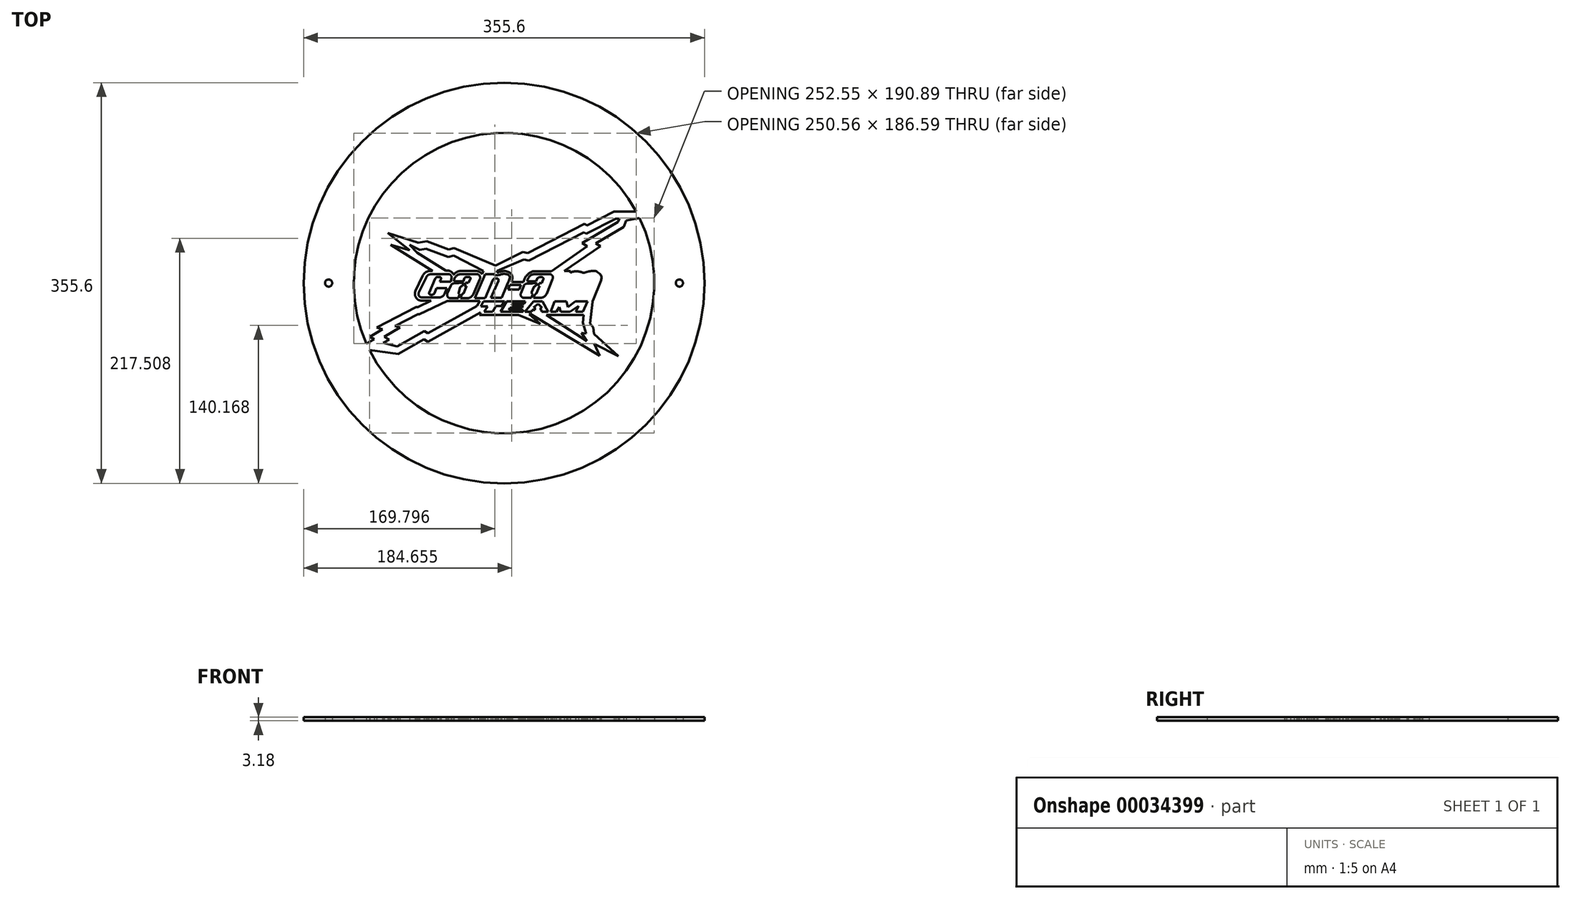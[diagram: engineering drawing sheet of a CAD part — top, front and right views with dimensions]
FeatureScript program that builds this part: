
annotation { "Feature Type Name" : "Feature", "Feature Type Description" : "" }
export const myFeature = defineFeature(function(context is Context, id is Id, definition is map)
    precondition{}
    {
        {
            var Q0;
            Q0=qCreatedBy(makeId("Top.planeOp"),FACE);
            var sketch = newSketch(context, id + "F0", { "sketchPlane" : qUnion([Q0])});
            skCircle(sketch, "E0", {"center": v(0, -177.8) * mm, "radius": 177.8 * mm});
            skArc(sketch, "E1.0", {"start": v(117.28, -114.33) * mm, "mid": v(-58.58, -58) * mm, "end": v(-122.11, -231.38) * mm});
            skLineSegment(sketch, "E2", {"start": v(-72.26, -171.41) * mm, "end": v(-78.52, -184.98) * mm});
            skLineSegment(sketch, "E3", {"start": v(117.28, -114.33) * mm, "end": v(97.65, -114.33) * mm});
            skLineSegment(sketch, "E4", {"start": v(97.65, -114.33) * mm, "end": v(73.49, -126.6) * mm});
            skLineSegment(sketch, "E5", {"start": v(73.49, -126.6) * mm, "end": v(71.57, -125.24) * mm});
            skLineSegment(sketch, "E6", {"start": v(71.57, -125.24) * mm, "end": v(21.06, -151.12) * mm});
            skLineSegment(sketch, "E7", {"start": v(21.06, -151.12) * mm, "end": v(16.63, -150.13) * mm});
            skLineSegment(sketch, "E8", {"start": v(16.63, -150.13) * mm, "end": v(-7.54, -162.28) * mm});
            skLineSegment(sketch, "E9", {"start": v(-7.54, -162.28) * mm, "end": v(-44.28, -146.75) * mm});
            skLineSegment(sketch, "E10", {"start": v(-44.28, -146.75) * mm, "end": v(-49.08, -148.1) * mm});
            skLineSegment(sketch, "E11", {"start": v(-49.08, -148.1) * mm, "end": v(-68.43, -140.65) * mm});
            skLineSegment(sketch, "E12", {"start": v(-68.43, -140.65) * mm, "end": v(-76.04, -142.13) * mm});
            skLineSegment(sketch, "E13", {"start": v(-76.04, -142.13) * mm, "end": v(-102.97, -133.39) * mm});
            skLineSegment(sketch, "E14", {"start": v(-102.97, -133.39) * mm, "end": v(-83.66, -148.7) * mm});
            skLineSegment(sketch, "E15", {"start": v(-83.66, -148.7) * mm, "end": v(-100.42, -143.93) * mm});
            skLineSegment(sketch, "E16", {"start": v(-100.42, -143.93) * mm, "end": v(-63.27, -167) * mm});
            skLineSegment(sketch, "E17", {"start": v(-63.27, -167) * mm, "end": v(-65.35, -167) * mm});
            skArc(sketch, "E18", {"start": v(-65.35, -167) * mm, "mid": v(-69.45, -168.2) * mm, "end": v(-72.26, -171.41) * mm});
            skLineSegment(sketch, "E19", {"start": v(-64.55, -193.44) * mm, "end": v(-73.1, -193.44) * mm});
            skArc(sketch, "E20", {"start": v(-78.52, -184.98) * mm, "mid": v(-78.13, -190.7) * mm, "end": v(-73.1, -193.44) * mm});
            skLineSegment(sketch, "E21", {"start": v(-107.77, -218.97) * mm, "end": v(-112.88, -217.3) * mm});
            skLineSegment(sketch, "E22", {"start": v(-107.77, -218.97) * mm, "end": v(-119.02, -225.44) * mm});
            skLineSegment(sketch, "E23", {"start": v(-119.02, -225.44) * mm, "end": v(-115.05, -227.68) * mm});
            skLineSegment(sketch, "E24", {"start": v(-119.42, -237.14) * mm, "end": v(-93.78, -240.85) * mm});
            skLineSegment(sketch, "E25", {"start": v(-93.78, -240.85) * mm, "end": v(-70.85, -227.83) * mm});
            skLineSegment(sketch, "E26", {"start": v(-70.85, -227.83) * mm, "end": v(-67.64, -229.84) * mm});
            skLineSegment(sketch, "E27", {"start": v(-67.64, -229.84) * mm, "end": v(-20.79, -203.8) * mm});
            skLineSegment(sketch, "E28", {"start": v(-20.79, -203.8) * mm, "end": v(-21.82, -205.96) * mm});
            skLineSegment(sketch, "E29", {"start": v(-21.82, -205.96) * mm, "end": v(12.97, -205.96) * mm});
            skLineSegment(sketch, "E30", {"start": v(85.4, -145.02) * mm, "end": v(53.44, -167.15) * mm});
            skLineSegment(sketch, "E31", {"start": v(85.4, -145.02) * mm, "end": v(81.53, -142.54) * mm});
            skLineSegment(sketch, "E32", {"start": v(81.53, -142.54) * mm, "end": v(106.14, -127.9) * mm});
            skLineSegment(sketch, "E33", {"start": v(106.14, -127.9) * mm, "end": v(108.41, -122.44) * mm});
            skLineSegment(sketch, "E34", {"start": v(108.41, -122.44) * mm, "end": v(120.17, -119.99) * mm});
            skArc(sketch, "E35.trimOffspring", {"start": v(-119.42, -237.14) * mm, "mid": v(58.58, -297.6) * mm, "end": v(120.17, -119.99) * mm});
            skLineSegment(sketch, "E36", {"start": v(-115.05, -227.68) * mm, "end": v(-122.11, -231.38) * mm});
            skLineSegment(sketch, "E37", {"start": v(-64.55, -193.44) * mm, "end": v(-76.52, -199) * mm});
            skLineSegment(sketch, "E38", {"start": v(-76.52, -199) * mm, "end": v(-77.85, -199) * mm});
            skLineSegment(sketch, "E39", {"start": v(-77.85, -199) * mm, "end": v(-112.88, -217.3) * mm});
            skLineSegment(sketch, "E40", {"start": v(12.97, -205.96) * mm, "end": v(32.12, -214.14) * mm});
            skLineSegment(sketch, "E41", {"start": v(32.12, -214.14) * mm, "end": v(22.38, -205.4) * mm});
            skLineSegment(sketch, "E42", {"start": v(22.38, -205.4) * mm, "end": v(23.2, -205.1) * mm});
            skLineSegment(sketch, "E43", {"start": v(23.2, -205.1) * mm, "end": v(84.9, -242.25) * mm});
            skLineSegment(sketch, "E44", {"start": v(84.9, -242.25) * mm, "end": v(80.04, -231.96) * mm});
            skLineSegment(sketch, "E45", {"start": v(76.25, -213.75) * mm, "end": v(78.4, -194.42) * mm});
            skLineSegment(sketch, "E46", {"start": v(78.7, -193.29) * mm, "end": v(86, -175.37) * mm});
            skLineSegment(sketch, "E47", {"start": v(53.44, -167.15) * mm, "end": v(58.86, -167.15) * mm});
            skLineSegment(sketch, "E48", {"start": v(58.86, -167.15) * mm, "end": v(58.86, -168.66) * mm});
            skArc(sketch, "E49", {"start": v(70.01, -168.75) * mm, "mid": v(64.45, -167.37) * mm, "end": v(58.86, -168.66) * mm});
            skFitSpline(sketch, "E50", {"points": [v(70.01, -168.75) * mm, v(76.95, -167.16) * mm, v(82.12, -167.61) * mm, v(86.22, -171.54) * mm, v(86, -175.37) * mm], "startDerivative": vector(25.34, 5.48) * mm, "endDerivative": vector(-7.42, -18.3) * mm});
            skLineSegment(sketch, "E51.0", {"start": v(-67.47, -222.43) * mm, "end": v(-23.9, -198.21) * mm});
            skLineSegment(sketch, "E51.1", {"start": v(-70.72, -220.4) * mm, "end": v(-67.47, -222.43) * mm});
            skLineSegment(sketch, "E51.2", {"start": v(-94.7, -234.01) * mm, "end": v(-70.72, -220.4) * mm});
            skLineSegment(sketch, "E52.0", {"start": v(-101.76, -227.87) * mm, "end": v(-107.29, -230.78) * mm});
            skLineSegment(sketch, "E52.1", {"start": v(-106.18, -225.38) * mm, "end": v(-101.76, -227.87) * mm});
            skLineSegment(sketch, "E52.2", {"start": v(-92.25, -217.37) * mm, "end": v(-106.18, -225.38) * mm});
            skLineSegment(sketch, "E52.3", {"start": v(-50.27, -193.82) * mm, "end": v(-75.12, -205.35) * mm});
            skLineSegment(sketch, "E52.4", {"start": v(-75.12, -205.35) * mm, "end": v(-76.3, -205.35) * mm});
            skLineSegment(sketch, "E52.5", {"start": v(-76.3, -205.35) * mm, "end": v(-96.6, -215.95) * mm});
            skLineSegment(sketch, "E52.6", {"start": v(-92.25, -217.37) * mm, "end": v(-96.6, -215.95) * mm});
            skLineSegment(sketch, "E53.trimOffspring", {"start": v(-107.29, -230.78) * mm, "end": v(-94.7, -234.01) * mm});
            skLineSegment(sketch, "E54.0", {"start": v(73.94, -145.23) * mm, "end": v(42.04, -167.32) * mm});
            skLineSegment(sketch, "E54.2", {"start": v(101.09, -123.52) * mm, "end": v(102.27, -120.68) * mm});
            skLineSegment(sketch, "E54.3", {"start": v(69.42, -142.35) * mm, "end": v(101.09, -123.52) * mm});
            skLineSegment(sketch, "E54.4", {"start": v(73.94, -145.23) * mm, "end": v(69.42, -142.35) * mm});
            skLineSegment(sketch, "E55.0", {"start": v(-69.01, -147.23) * mm, "end": v(-74.83, -148.36) * mm});
            skLineSegment(sketch, "E55.1", {"start": v(-49.39, -154.78) * mm, "end": v(-69.01, -147.23) * mm});
            skLineSegment(sketch, "E55.2", {"start": v(-44.7, -153.46) * mm, "end": v(-49.39, -154.78) * mm});
            skLineSegment(sketch, "E55.3", {"start": v(-18.2, -167.21) * mm, "end": v(-44.7, -153.46) * mm});
            skLineSegment(sketch, "E55.4", {"start": v(17.46, -156.82) * mm, "end": v(-6.17, -167.21) * mm});
            skLineSegment(sketch, "E55.5", {"start": v(21.92, -157.81) * mm, "end": v(17.46, -156.82) * mm});
            skLineSegment(sketch, "E55.7", {"start": v(99.17, -120.68) * mm, "end": v(72.95, -133.99) * mm});
            skLineSegment(sketch, "E55.8", {"start": v(72.95, -133.99) * mm, "end": v(71.04, -132.64) * mm});
            skLineSegment(sketch, "E55.9", {"start": v(71.04, -132.64) * mm, "end": v(21.92, -157.81) * mm});
            skLineSegment(sketch, "E56.trimOffspring", {"start": v(102.27, -120.68) * mm, "end": v(99.17, -120.68) * mm});
            skLineSegment(sketch, "E57.0", {"start": v(-77.12, -150.92) * mm, "end": v(-51.5, -166.82) * mm});
            skLineSegment(sketch, "E58", {"start": v(-18.2, -167.21) * mm, "end": v(-6.17, -167.21) * mm});
            skLineSegment(sketch, "E59", {"start": v(-77.12, -150.92) * mm, "end": v(-83.81, -143.85) * mm});
            skLineSegment(sketch, "E60", {"start": v(-83.81, -143.85) * mm, "end": v(-74.83, -148.36) * mm});
            skLineSegment(sketch, "E61", {"start": v(-51.5, -166.82) * mm, "end": v(-49.7, -166.82) * mm});
            skLineSegment(sketch, "E62", {"start": v(-38.6, -167.12) * mm, "end": v(-24.39, -167.12) * mm});
            skLineSegment(sketch, "E63", {"start": v(25.57, -167.32) * mm, "end": v(42.04, -167.32) * mm});
            skLineSegment(sketch, "E64", {"start": v(-44.94, -170.34) * mm, "end": v(-44.36, -170.34) * mm});
            skArc(sketch, "E65", {"start": v(-38.6, -167.12) * mm, "mid": v(-41.9, -167.98) * mm, "end": v(-44.36, -170.34) * mm});
            skArc(sketch, "E66", {"start": v(-44.94, -170.34) * mm, "mid": v(-46.74, -167.8) * mm, "end": v(-49.7, -166.82) * mm});
            skLineSegment(sketch, "E67", {"start": v(-18.2, -167.21) * mm, "end": v(-19.63, -169.96) * mm});
            skArc(sketch, "E68", {"start": v(-19.63, -169.96) * mm, "mid": v(-21.62, -167.88) * mm, "end": v(-24.39, -167.12) * mm});
            skLineSegment(sketch, "E69", {"start": v(-6.17, -167.21) * mm, "end": v(-6.17, -168.44) * mm});
            skLineSegment(sketch, "E70", {"start": v(17.18, -176.77) * mm, "end": v(6.63, -176.77) * mm});
            skLineSegment(sketch, "E71", {"start": v(6.63, -176.77) * mm, "end": v(7.12, -175.68) * mm});
            skLineSegment(sketch, "E72", {"start": v(17.18, -176.77) * mm, "end": v(17.56, -175.58) * mm});
            skArc(sketch, "E73", {"start": v(25.57, -167.32) * mm, "mid": v(20.6, -170.52) * mm, "end": v(17.56, -175.58) * mm});
            skFitSpline(sketch, "E74", {"points": [v(-6.17, -168.44) * mm, v(-1.73, -167.3) * mm, v(3.35, -167.7) * mm, v(7.07, -170.88) * mm, v(7.12, -175.68) * mm], "startDerivative": vector(17.75, 5.69) * mm, "endDerivative": vector(-3.32, -20.38) * mm});
            skLineSegment(sketch, "E75", {"start": v(-50.27, -193.82) * mm, "end": v(-21.3, -193.82) * mm});
            skLineSegment(sketch, "E76", {"start": v(-21.3, -193.82) * mm, "end": v(-23.9, -198.21) * mm});
            skLineSegment(sketch, "E77", {"start": v(-18.13, -194) * mm, "end": v(-20.4, -198.54) * mm});
            skLineSegment(sketch, "E78", {"start": v(-20.4, -198.54) * mm, "end": v(-14.6, -198.54) * mm});
            skLineSegment(sketch, "E79", {"start": v(-14.6, -198.54) * mm, "end": v(-17.8, -203.32) * mm});
            skLineSegment(sketch, "E80", {"start": v(-17.8, -203.32) * mm, "end": v(-10.12, -203.32) * mm});
            skLineSegment(sketch, "E81", {"start": v(-10.12, -203.32) * mm, "end": v(-7.03, -198.16) * mm});
            skLineSegment(sketch, "E82", {"start": v(-7.03, -198.16) * mm, "end": v(-2.13, -198.16) * mm});
            skLineSegment(sketch, "E83", {"start": v(-2.13, -198.16) * mm, "end": v(0.4, -194) * mm});
            skLineSegment(sketch, "E84", {"start": v(0.4, -194) * mm, "end": v(-18.13, -194) * mm});
            skLineSegment(sketch, "E85", {"start": v(2.48, -194) * mm, "end": v(-3.15, -203.32) * mm});
            skLineSegment(sketch, "E86", {"start": v(-3.15, -203.32) * mm, "end": v(16.87, -203.32) * mm});
            skLineSegment(sketch, "E87", {"start": v(16.87, -203.32) * mm, "end": v(16.87, -201.77) * mm});
            skLineSegment(sketch, "E88", {"start": v(16.87, -201.77) * mm, "end": v(4.38, -201.77) * mm});
            skLineSegment(sketch, "E89", {"start": v(4.38, -201.77) * mm, "end": v(5.34, -199.65) * mm});
            skLineSegment(sketch, "E90", {"start": v(5.34, -199.65) * mm, "end": v(16.08, -199.65) * mm});
            skLineSegment(sketch, "E91", {"start": v(16.08, -199.65) * mm, "end": v(16.55, -197.7) * mm});
            skLineSegment(sketch, "E92", {"start": v(16.55, -197.7) * mm, "end": v(6.6, -197.7) * mm});
            skLineSegment(sketch, "E93", {"start": v(6.6, -197.7) * mm, "end": v(7.31, -196.37) * mm});
            skLineSegment(sketch, "E94", {"start": v(7.31, -196.37) * mm, "end": v(18.05, -196.37) * mm});
            skLineSegment(sketch, "E95", {"start": v(18.05, -196.37) * mm, "end": v(18.95, -194) * mm});
            skLineSegment(sketch, "E96", {"start": v(18.95, -194) * mm, "end": v(2.48, -194) * mm});
            skLineSegment(sketch, "E97", {"start": v(69.83, -203.32) * mm, "end": v(74.1, -194) * mm});
            skLineSegment(sketch, "E98", {"start": v(74.1, -194) * mm, "end": v(63.27, -194) * mm});
            skLineSegment(sketch, "E99", {"start": v(63.27, -194) * mm, "end": v(56.5, -199.18) * mm});
            skLineSegment(sketch, "E100", {"start": v(56.5, -199.18) * mm, "end": v(55.3, -194) * mm});
            skLineSegment(sketch, "E101", {"start": v(55.3, -194) * mm, "end": v(45.02, -194) * mm});
            skLineSegment(sketch, "E102", {"start": v(45.02, -194) * mm, "end": v(41.36, -203.32) * mm});
            skLineSegment(sketch, "E103", {"start": v(41.36, -203.32) * mm, "end": v(46.39, -203.32) * mm});
            skLineSegment(sketch, "E104", {"start": v(46.39, -203.32) * mm, "end": v(49.03, -199.1) * mm});
            skLineSegment(sketch, "E105", {"start": v(49.03, -199.1) * mm, "end": v(50.44, -203.32) * mm});
            skLineSegment(sketch, "E106", {"start": v(50.44, -203.32) * mm, "end": v(58.7, -203.32) * mm});
            skLineSegment(sketch, "E107", {"start": v(58.7, -203.32) * mm, "end": v(66.2, -198.05) * mm});
            skLineSegment(sketch, "E108", {"start": v(66.2, -198.05) * mm, "end": v(63.52, -203.32) * mm});
            skLineSegment(sketch, "E109", {"start": v(63.52, -203.32) * mm, "end": v(69.83, -203.32) * mm});
            skLineSegment(sketch, "E110", {"start": v(26.29, -194) * mm, "end": v(33.99, -194) * mm});
            skLineSegment(sketch, "E111", {"start": v(33.99, -194) * mm, "end": v(39.1, -203.32) * mm});
            skLineSegment(sketch, "E112", {"start": v(39.1, -203.32) * mm, "end": v(33.53, -203.32) * mm});
            skLineSegment(sketch, "E113", {"start": v(33.53, -203.32) * mm, "end": v(33.3, -201.56) * mm});
            skLineSegment(sketch, "E114", {"start": v(33.3, -201.56) * mm, "end": v(32.38, -201.56) * mm});
            skLineSegment(sketch, "E115", {"start": v(24.97, -201.59) * mm, "end": v(24.58, -203.32) * mm});
            skLineSegment(sketch, "E116", {"start": v(24.58, -203.32) * mm, "end": v(18.6, -203.32) * mm});
            skLineSegment(sketch, "E117", {"start": v(18.6, -203.32) * mm, "end": v(26.29, -194) * mm});
            skLineSegment(sketch, "E118", {"start": v(-61.04, -174.2) * mm, "end": v(-66.34, -186.14) * mm});
            skLineSegment(sketch, "E119", {"start": v(-56.97, -176.49) * mm, "end": v(-47.2, -176.49) * mm});
            skLineSegment(sketch, "E120", {"start": v(-59.82, -182.46) * mm, "end": v(-50.67, -182.46) * mm});
            skLineSegment(sketch, "E121", {"start": v(-59.82, -182.46) * mm, "end": v(-61.85, -187.06) * mm});
            skLineSegment(sketch, "E122", {"start": v(-56.97, -176.49) * mm, "end": v(-56.1, -174.53) * mm});
            skLineSegment(sketch, "E123", {"start": v(-44.45, -176.35) * mm, "end": v(-36.19, -176.35) * mm});
            skLineSegment(sketch, "E124", {"start": v(-36.19, -176.35) * mm, "end": v(-35.02, -173.47) * mm});
            skLineSegment(sketch, "E125", {"start": v(-47.23, -180.01) * mm, "end": v(-50.26, -187.18) * mm});
            skLineSegment(sketch, "E126", {"start": v(-33.33, -180.45) * mm, "end": v(-35.06, -180.45) * mm});
            skLineSegment(sketch, "E127", {"start": v(-35.85, -186.76) * mm, "end": v(-33.33, -180.45) * mm});
            skLineSegment(sketch, "E128", {"start": v(-50.67, -182.46) * mm, "end": v(-52.45, -186.93) * mm});
            skLineSegment(sketch, "E129", {"start": v(-57.82, -190.58) * mm, "end": v(-72.85, -190.58) * mm});
            skLineSegment(sketch, "E130", {"start": v(-69.15, -173.18) * mm, "end": v(-75.47, -185.94) * mm});
            skLineSegment(sketch, "E131", {"start": v(-49.41, -169.86) * mm, "end": v(-64.53, -169.86) * mm});
            skLineSegment(sketch, "E132", {"start": v(-32.59, -191.24) * mm, "end": v(-38.7, -191.24) * mm});
            skLineSegment(sketch, "E133", {"start": v(-16.76, -169.96) * mm, "end": v(-25.99, -191.11) * mm});
            skLineSegment(sketch, "E134", {"start": v(-25.99, -191.11) * mm, "end": v(-16.86, -191.11) * mm});
            skLineSegment(sketch, "E135", {"start": v(-16.86, -191.11) * mm, "end": v(-10, -175.33) * mm});
            skLineSegment(sketch, "E136", {"start": v(-16.76, -169.96) * mm, "end": v(-8.06, -169.96) * mm});
            skLineSegment(sketch, "E137", {"start": v(-8.06, -169.96) * mm, "end": v(-8.06, -171.15) * mm});
            skLineSegment(sketch, "E138", {"start": v(-5.04, -175.92) * mm, "end": v(-11.75, -190.95) * mm});
            skLineSegment(sketch, "E139", {"start": v(-11.75, -190.95) * mm, "end": v(-2, -190.96) * mm});
            skLineSegment(sketch, "E140", {"start": v(-2, -190.96) * mm, "end": v(3.63, -177.12) * mm});
            skLineSegment(sketch, "E141", {"start": v(5.17, -179.48) * mm, "end": v(3.56, -183.42) * mm});
            skLineSegment(sketch, "E142", {"start": v(3.56, -183.42) * mm, "end": v(13.37, -183.42) * mm});
            skLineSegment(sketch, "E143", {"start": v(13.37, -183.42) * mm, "end": v(14.9, -179.48) * mm});
            skLineSegment(sketch, "E144", {"start": v(14.9, -179.48) * mm, "end": v(5.17, -179.48) * mm});
            skLineSegment(sketch, "E145", {"start": v(28.38, -176.26) * mm, "end": v(20.68, -176.26) * mm});
            skLineSegment(sketch, "E146", {"start": v(29.8, -173.52) * mm, "end": v(28.38, -176.26) * mm});
            skLineSegment(sketch, "E147", {"start": v(34.76, -174.74) * mm, "end": v(33.45, -177.78) * mm});
            skLineSegment(sketch, "E148", {"start": v(33.45, -177.78) * mm, "end": v(31.35, -177.88) * mm});
            skLineSegment(sketch, "E149", {"start": v(32.47, -190.85) * mm, "end": v(26.17, -190.85) * mm});
            skLineSegment(sketch, "E150", {"start": v(17.47, -180.38) * mm, "end": v(14.91, -186.9) * mm});
            skLineSegment(sketch, "E151", {"start": v(27.3, -169.91) * mm, "end": v(40.33, -169.91) * mm});
            skLineSegment(sketch, "E152", {"start": v(43.13, -174.28) * mm, "end": v(37.77, -187.3) * mm});
            skLineSegment(sketch, "E153", {"start": v(57.07, -169.62) * mm, "end": v(47.63, -169.62) * mm});
            skLineSegment(sketch, "E154", {"start": v(47.63, -169.62) * mm, "end": v(38, -190.94) * mm});
            skLineSegment(sketch, "E155", {"start": v(38, -190.94) * mm, "end": v(48.29, -190.94) * mm});
            skLineSegment(sketch, "E156", {"start": v(48.29, -190.94) * mm, "end": v(55.17, -175.46) * mm});
            skLineSegment(sketch, "E157", {"start": v(83.54, -174.33) * mm, "end": v(76.73, -191.01) * mm});
            skLineSegment(sketch, "E158", {"start": v(76.73, -191.01) * mm, "end": v(67.59, -191.01) * mm});
            skLineSegment(sketch, "E159", {"start": v(67.59, -191.01) * mm, "end": v(74.26, -175.97) * mm});
            skLineSegment(sketch, "E160", {"start": v(69.23, -174.97) * mm, "end": v(62.4, -191.01) * mm});
            skLineSegment(sketch, "E161", {"start": v(62.4, -191.01) * mm, "end": v(53.4, -191.01) * mm});
            skLineSegment(sketch, "E162", {"start": v(53.4, -191.01) * mm, "end": v(59.88, -176.01) * mm});
            skFitSpline(sketch, "E163.0", {"points": [v(70.58, -171.37) * mm, v(71.7, -171.13) * mm, v(73.3, -170.71) * mm, v(75.27, -170.22) * mm, v(76.64, -169.92) * mm, v(77.87, -169.72) * mm, v(78.93, -169.64) * mm, v(79.82, -169.69) * mm, v(80.49, -169.84) * mm, v(81, -170.04) * mm, v(81.42, -170.25) * mm, v(81.86, -170.51) * mm, v(82.43, -170.93) * mm, v(82.95, -171.41) * mm, v(83.35, -171.9) * mm, v(83.58, -172.23) * mm, v(83.7, -172.46) * mm, v(83.76, -172.6) * mm, v(83.8, -172.73) * mm, v(83.83, -172.88) * mm, v(83.85, -173.14) * mm, v(83.8, -173.57) * mm, v(83.64, -174.08) * mm, v(83.53, -174.36) * mm]});
            skLineSegment(sketch, "E164", {"start": v(57.07, -169.62) * mm, "end": v(57.07, -170.6) * mm});
            skArc(sketch, "E165.0", {"start": v(70.58, -171.37) * mm, "mid": v(65.56, -169.36) * mm, "end": v(60.21, -170.15) * mm});
            skFitSpline(sketch, "E166", {"points": [v(57.07, -170.6) * mm, v(58.77, -170.52) * mm, v(60.21, -170.15) * mm], "startDerivative": vector(3.13, 1.09) * mm, "endDerivative": vector(2.94, 0.71) * mm});
            skArc(sketch, "E167", {"start": v(27.3, -169.91) * mm, "mid": v(22.71, -171.75) * mm, "end": v(20.68, -176.26) * mm});
            skArc(sketch, "E168", {"start": v(43.13, -174.28) * mm, "mid": v(42.93, -171.33) * mm, "end": v(40.33, -169.91) * mm});
            skArc(sketch, "E169", {"start": v(32.47, -190.85) * mm, "mid": v(35.66, -189.88) * mm, "end": v(37.77, -187.3) * mm});
            skArc(sketch, "E170", {"start": v(14.91, -186.9) * mm, "mid": v(15.4, -189.86) * mm, "end": v(18.23, -190.85) * mm});
            skArc(sketch, "E171", {"start": v(21.18, -178.39) * mm, "mid": v(18.96, -178.7) * mm, "end": v(17.47, -180.38) * mm});
            skLineSegment(sketch, "E172", {"start": v(31.9, -172.58) * mm, "end": v(33.51, -172.58) * mm});
            skArc(sketch, "E173", {"start": v(34.76, -174.74) * mm, "mid": v(34.76, -173.3) * mm, "end": v(33.51, -172.58) * mm});
            skArc(sketch, "E174", {"start": v(31.9, -172.58) * mm, "mid": v(30.75, -172.83) * mm, "end": v(29.8, -173.52) * mm});
            skArc(sketch, "E175", {"start": v(-50.26, -187.18) * mm, "mid": v(-50, -189.93) * mm, "end": v(-47.57, -191.24) * mm});
            skArc(sketch, "E176", {"start": v(-57.82, -190.58) * mm, "mid": v(-54.58, -189.58) * mm, "end": v(-52.45, -186.93) * mm});
            skArc(sketch, "E177", {"start": v(-75.47, -185.94) * mm, "mid": v(-75.51, -189.02) * mm, "end": v(-72.85, -190.58) * mm});
            skArc(sketch, "E178", {"start": v(-64.53, -169.86) * mm, "mid": v(-67.38, -170.78) * mm, "end": v(-69.15, -173.18) * mm});
            skLineSegment(sketch, "E179", {"start": v(-58.8, -172.42) * mm, "end": v(-57.14, -172.42) * mm});
            skLineSegment(sketch, "E180", {"start": v(-46.56, -173.37) * mm, "end": v(-47.2, -176.49) * mm});
            skLineSegment(sketch, "E181", {"start": v(-31.54, -177.45) * mm, "end": v(-34.1, -177.6) * mm});
            skLineSegment(sketch, "E182", {"start": v(-37.9, -169.86) * mm, "end": v(-24.4, -169.86) * mm});
            skLineSegment(sketch, "E183", {"start": v(-21.41, -174.4) * mm, "end": v(-27.12, -187.64) * mm});
            skLineSegment(sketch, "E184", {"start": v(70.96, -173.83) * mm, "end": v(72.87, -173.83) * mm});
            skLineSegment(sketch, "E185", {"start": v(57.37, -174.03) * mm, "end": v(58.57, -174.03) * mm});
            skArc(sketch, "E186", {"start": v(57.37, -174.03) * mm, "mid": v(56.06, -174.42) * mm, "end": v(55.17, -175.46) * mm});
            skArc(sketch, "E187", {"start": v(59.88, -176.01) * mm, "mid": v(59.76, -174.67) * mm, "end": v(58.57, -174.03) * mm});
            skArc(sketch, "E188", {"start": v(70.96, -173.83) * mm, "mid": v(69.92, -174.14) * mm, "end": v(69.23, -174.97) * mm});
            skArc(sketch, "E189", {"start": v(74.26, -175.97) * mm, "mid": v(74.15, -174.52) * mm, "end": v(72.87, -173.83) * mm});
            skLineSegment(sketch, "E190", {"start": v(-7.84, -173.68) * mm, "end": v(-6.5, -173.68) * mm});
            skArc(sketch, "E191", {"start": v(-7.84, -173.68) * mm, "mid": v(-9.2, -174.14) * mm, "end": v(-10, -175.33) * mm});
            skArc(sketch, "E192", {"start": v(-5.04, -175.92) * mm, "mid": v(-5.16, -174.4) * mm, "end": v(-6.5, -173.68) * mm});
            skFitSpline(sketch, "E193", {"points": [v(-8.06, -171.15) * mm, v(-4.05, -170.48) * mm, v(-0.72, -169.73) * mm, v(2.82, -170.16) * mm, v(5.08, -172.14) * mm, v(3.63, -177.12) * mm], "startDerivative": vector(20.02, 2.73) * mm, "endDerivative": vector(-11.42, -23.85) * mm});
            skArc(sketch, "E194", {"start": v(-37.9, -169.86) * mm, "mid": v(-42.5, -171.76) * mm, "end": v(-44.45, -176.35) * mm});
            skArc(sketch, "E195", {"start": v(-21.41, -174.4) * mm, "mid": v(-21.68, -171.33) * mm, "end": v(-24.4, -169.86) * mm});
            skArc(sketch, "E196", {"start": v(-32.59, -191.24) * mm, "mid": v(-29.32, -190.26) * mm, "end": v(-27.12, -187.64) * mm});
            skArc(sketch, "E197", {"start": v(-44.64, -178.2) * mm, "mid": v(-46.2, -178.73) * mm, "end": v(-47.23, -180.01) * mm});
            skLineSegment(sketch, "E198", {"start": v(-31.54, -177.45) * mm, "end": v(-30.1, -174.57) * mm});
            skLineSegment(sketch, "E199", {"start": v(-33.04, -172.39) * mm, "end": v(-31.05, -172.39) * mm});
            skArc(sketch, "E200", {"start": v(-30.1, -174.57) * mm, "mid": v(-29.86, -173.17) * mm, "end": v(-31.05, -172.39) * mm});
            skArc(sketch, "E201", {"start": v(-33.04, -172.39) * mm, "mid": v(-34.22, -172.58) * mm, "end": v(-35.02, -173.47) * mm});
            skArc(sketch, "E202", {"start": v(-46.56, -173.37) * mm, "mid": v(-47.15, -170.93) * mm, "end": v(-49.41, -169.86) * mm});
            skArc(sketch, "E203", {"start": v(-56.1, -174.53) * mm, "mid": v(-55.96, -173.16) * mm, "end": v(-57.14, -172.42) * mm});
            skArc(sketch, "E204", {"start": v(-58.8, -172.42) * mm, "mid": v(-60.23, -172.92) * mm, "end": v(-61.04, -174.2) * mm});
            skLineSegment(sketch, "E205", {"start": v(-65, -188.2) * mm, "end": v(-63.76, -188.2) * mm});
            skArc(sketch, "E206", {"start": v(-63.76, -188.2) * mm, "mid": v(-62.65, -187.89) * mm, "end": v(-61.85, -187.06) * mm});
            skArc(sketch, "E207", {"start": v(-66.34, -186.14) * mm, "mid": v(-66.23, -187.53) * mm, "end": v(-65, -188.2) * mm});
            skLineSegment(sketch, "E208", {"start": v(-38.85, -181.8) * mm, "end": v(-40.31, -186.34) * mm});
            skLineSegment(sketch, "E209", {"start": v(-39.47, -187.5) * mm, "end": v(-39.15, -187.5) * mm});
            skArc(sketch, "E210", {"start": v(-37, -180.45) * mm, "mid": v(-38.15, -180.82) * mm, "end": v(-38.85, -181.8) * mm});
            skArc(sketch, "E211", {"start": v(-40.31, -186.34) * mm, "mid": v(-40.19, -187.13) * mm, "end": v(-39.47, -187.5) * mm});
            skArc(sketch, "E212", {"start": v(-36.93, -187.5) * mm, "mid": v(-36.28, -187.3) * mm, "end": v(-35.85, -186.76) * mm});
            skLineSegment(sketch, "E213", {"start": v(31.7, -180.45) * mm, "end": v(30.33, -180.45) * mm});
            skLineSegment(sketch, "E214", {"start": v(31.7, -180.45) * mm, "end": v(28.6, -187.07) * mm});
            skLineSegment(sketch, "E215", {"start": v(27.64, -187.67) * mm, "end": v(27.44, -187.67) * mm});
            skLineSegment(sketch, "E216", {"start": v(26.52, -181.36) * mm, "end": v(24.72, -185.82) * mm});
            skArc(sketch, "E217", {"start": v(27.87, -180.45) * mm, "mid": v(27.05, -180.7) * mm, "end": v(26.52, -181.36) * mm});
            skArc(sketch, "E218", {"start": v(27.64, -187.67) * mm, "mid": v(28.2, -187.5) * mm, "end": v(28.6, -187.07) * mm});
            skArc(sketch, "E219", {"start": v(24.72, -185.82) * mm, "mid": v(24.66, -186.83) * mm, "end": v(25.23, -187.67) * mm});
            skLineSegment(sketch, "E220", {"start": v(30.14, -196.27) * mm, "end": v(26.08, -199.47) * mm});
            skLineSegment(sketch, "E221", {"start": v(33.89, -199.83) * mm, "end": v(30.14, -196.27) * mm});
            skLineSegment(sketch, "E222", {"start": v(32.38, -201.56) * mm, "end": v(32.38, -199.73) * mm});
            skLineSegment(sketch, "E223", {"start": v(27.44, -201.56) * mm, "end": v(27.44, -199.4) * mm});
            skLineSegment(sketch, "E224.trimOffspring", {"start": v(32.38, -199.73) * mm, "end": v(33.89, -199.83) * mm});
            skLineSegment(sketch, "E225", {"start": v(29.5, -177.97) * mm, "end": v(28.48, -180.45) * mm});
            skLineSegment(sketch, "E226", {"start": v(31.35, -177.88) * mm, "end": v(30.33, -180.45) * mm});
            skLineSegment(sketch, "E227", {"start": v(-35.7, -177.69) * mm, "end": v(-36.67, -180.45) * mm});
            skLineSegment(sketch, "E228", {"start": v(-34.1, -177.6) * mm, "end": v(-35.06, -180.45) * mm});
            skLineSegment(sketch, "E229.trimOffspring", {"start": v(-35.7, -177.69) * mm, "end": v(-44.64, -178.2) * mm});
            skLineSegment(sketch, "E230.trimOffspring", {"start": v(-37.43, -187.5) * mm, "end": v(-36.93, -187.5) * mm});
            skLineSegment(sketch, "E231", {"start": v(-37, -180.45) * mm, "end": v(-36.67, -180.45) * mm});
            skLineSegment(sketch, "E232.trimOffspring", {"start": v(-39.15, -187.5) * mm, "end": v(-40.47, -191.24) * mm});
            skLineSegment(sketch, "E233.trimOffspring", {"start": v(-37.43, -187.5) * mm, "end": v(-38.7, -191.24) * mm});
            skLineSegment(sketch, "E234.trimOffspring", {"start": v(-40.47, -191.24) * mm, "end": v(-47.57, -191.24) * mm});
            skLineSegment(sketch, "E235.trimOffspring", {"start": v(24.23, -190.85) * mm, "end": v(18.23, -190.85) * mm});
            skLineSegment(sketch, "E236.trimOffspring", {"start": v(28.48, -180.45) * mm, "end": v(27.87, -180.45) * mm});
            skLineSegment(sketch, "E237.trimOffspring", {"start": v(29.5, -177.97) * mm, "end": v(21.18, -178.39) * mm});
            skLineSegment(sketch, "E238.trimOffspring", {"start": v(25.53, -187.67) * mm, "end": v(25.23, -187.67) * mm});
            skLineSegment(sketch, "E239.trimOffspring", {"start": v(25.53, -187.67) * mm, "end": v(24.23, -190.85) * mm});
            skLineSegment(sketch, "E240.trimOffspring", {"start": v(27.44, -187.67) * mm, "end": v(26.17, -190.85) * mm});
            skLineSegment(sketch, "E241", {"start": v(0, -355.6) * mm, "end": v(0, 0) * mm, "construction": true});
            skLineSegment(sketch, "E242", {"start": v(-177.8, -177.8) * mm, "end": v(-133.35, -177.8) * mm, "construction": true});
            skCircle(sketch, "E243", {"center": v(-155.58, -177.8) * mm, "radius": 3.18 * mm});
            skCircle(sketch, "E244.MirrorC", {"center": v(155.58, -177.8) * mm, "radius": 3.18 * mm});
            skLineSegment(sketch, "E245", {"start": v(80.04, -231.96) * mm, "end": v(101.26, -242.56) * mm});
            skLineSegment(sketch, "E246", {"start": v(101.26, -242.56) * mm, "end": v(79.85, -222.85) * mm});
            skLineSegment(sketch, "E247", {"start": v(79.85, -222.85) * mm, "end": v(79.24, -217.09) * mm});
            skLineSegment(sketch, "E248", {"start": v(79.24, -217.09) * mm, "end": v(76.25, -213.75) * mm});
            skLineSegment(sketch, "E249.0", {"start": v(72.85, -222.48) * mm, "end": v(69.95, -212.95) * mm});
            skLineSegment(sketch, "E249.1", {"start": v(68.75, -222.07) * mm, "end": v(72.85, -222.48) * mm});
            skLineSegment(sketch, "E250.1", {"start": v(73.53, -229.23) * mm, "end": v(68.75, -222.07) * mm});
            skLineSegment(sketch, "E251.0", {"start": v(69.95, -212.95) * mm, "end": v(70.71, -206.07) * mm});
            skPoint(sketch, "E252.orphan", {"position": v(73.53, -222.55) * mm});
            skLineSegment(sketch, "E253", {"start": v(70.71, -206.07) * mm, "end": v(62.7, -206.15) * mm});
            skLineSegment(sketch, "E254", {"start": v(62.7, -206.15) * mm, "end": v(37.7, -206.26) * mm});
            skLineSegment(sketch, "E255.trimOffspring", {"start": v(37.7, -206.26) * mm, "end": v(73.53, -229.23) * mm});
            skArc(sketch, "E256", {"start": v(78.7, -193.29) * mm, "mid": v(78.5, -193.84) * mm, "end": v(78.4, -194.42) * mm});
            skPoint(sketch, "E257", {"position": v(30.14, -194) * mm});
            skLineSegment(sketch, "E258", {"start": v(27.44, -201.56) * mm, "end": v(24.97, -201.59) * mm});
            skLineSegment(sketch, "E259", {"start": v(27.44, -199.4) * mm, "end": v(26.08, -199.47) * mm});
            skSolve(sketch);
        }
        {
            var Q0;
            Q0 = qSketchRegion(id + "F0", true);
            extrude(context, id + "F1", {"entities" : qUnion([Q0]), "depth" : 3.17 * mm});
        }
    });
